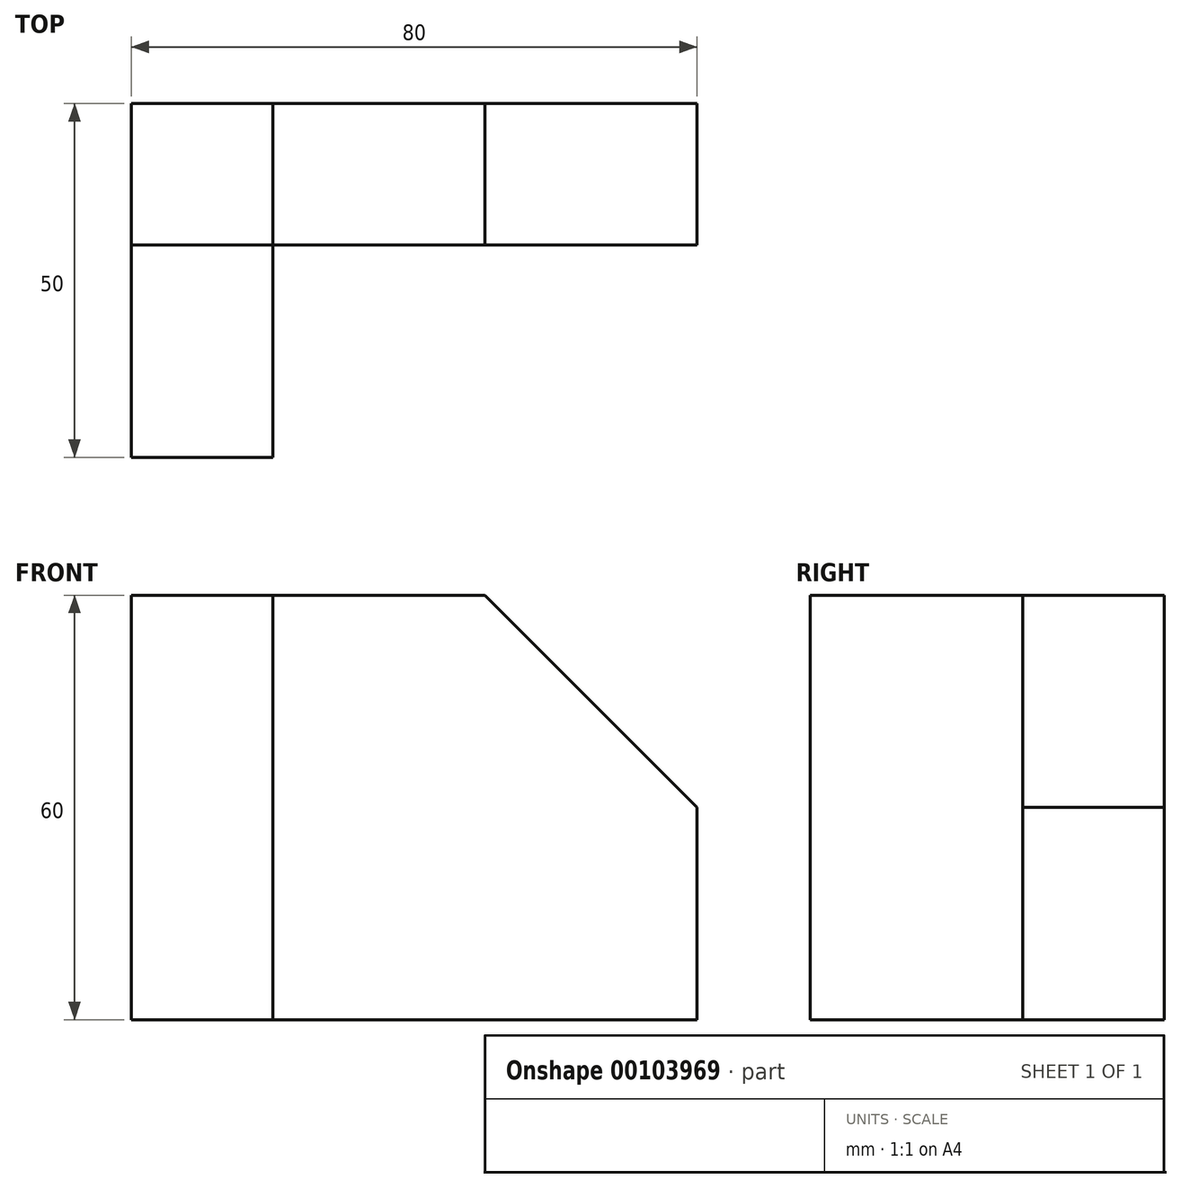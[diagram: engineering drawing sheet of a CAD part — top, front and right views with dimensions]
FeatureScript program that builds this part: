
annotation { "Feature Type Name" : "Feature", "Feature Type Description" : "" }
export const myFeature = defineFeature(function(context is Context, id is Id, definition is map)
    precondition{}
    {
        {
            var Q0;
            Q0=qCreatedBy(makeId("Front.planeOp"),FACE);
            var sketch = newSketch(context, id + "F0", { "sketchPlane" : qUnion([Q0])});
            skLineSegment(sketch, "E0.bottom", {"start": v(10, 30) * mm, "end": v(-40, 30) * mm});
            skLineSegment(sketch, "E0.top", {"start": v(40, -30) * mm, "end": v(-40, -30) * mm});
            skLineSegment(sketch, "E0.left", {"start": v(40, 0) * mm, "end": v(40, -30) * mm});
            skLineSegment(sketch, "E0.right", {"start": v(-40, 30) * mm, "end": v(-40, -30) * mm});
            skPoint(sketch, "E0.middle", {"position": v(0, 0) * mm});
            skLineSegment(sketch, "E1", {"start": v(-20, 30) * mm, "end": v(-20, -30) * mm});
            skLineSegment(sketch, "E2", {"start": v(22.58, 0) * mm, "end": v(51.61, 0) * mm});
            skLineSegment(sketch, "E3", {"start": v(10, 35.58) * mm, "end": v(10, 30) * mm});
            skLineSegment(sketch, "E4", {"start": v(10, 30) * mm, "end": v(40, 0) * mm});
            skPoint(sketch, "E5.orphan", {"position": v(40, 30) * mm});
            skSolve(sketch);
        }
        {
            var Q0;
            {var subQ0=sQuery(id+"F0.wireOp",EDGE,"E0.right");Q0=makeQuery(id+"F0.imprint","IMPRINT",FACE,{"disambiguationData":[TD([[makeQuery(id+"F0.imprint","IMPRINT",EDGE,{"derivedFrom":subQ0}),1.0]])]});}
            extrude(context, id + "F1", {"entities" : qUnion([Q0]), "depth" : 50 * mm, "offsetDistance" : 25 * mm});
        }
        {
            var Q0;
            Q0 = qSketchRegion(id + "F0", true);
            extrude(context, id + "F2", {"entities" : qUnion([Q0]), "depth" : 20 * mm, "offsetDistance" : 25 * mm});
        }
    });
